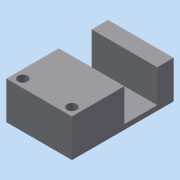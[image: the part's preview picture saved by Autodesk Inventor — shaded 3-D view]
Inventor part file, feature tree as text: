
AUTODESK INVENTOR PART (.ipt)
format: ipt  version: 2015 (Build 190159000, 159)  size: 111,616 bytes
history: native  units: mm
features: sketch x6, extrude x5, projected_geometry x2, hole x1
ambient origin geometry x8: Origin, YZ Plane, XZ Plane, XY Plane, X Axis, Y Axis, Z Axis, Center Point
bodies: Solid1 (feature_tree)
feature tree (14):
  extrude  "Extrusion1"  Depth=10.0mm
  hole  "Hole1"  [1 undecoded]
  extrude  "Extrusion2"  Depth=5.0mm
  extrude  "Extrusion3"  Depth=10.0mm TaperAngle=0.0deg
  extrude  "Extrusion4"  Depth=52.0mm TaperAngle=0.0deg
  extrude  "Extrusion5"  Depth=10.0mm
  sketch  "Sketch1"  dims[d0=40.0mm d1=10.0mm]
  sketch  "Sketch2"  dims[d2=10.0mm d3=0.0mm d4=30.0mm]
  sketch  "Sketch3"  dims[d5=5.0mm d6=5.0mm]
  projected_geometry  "Projected Loop1"
  sketch  "Sketch4"  dims[d7=5.0mm]
  sketch  "Sketch5"  dims[d8=6.0mm d9=6.0mm d10=4.0mm d11=2.0mm d12=90.0deg d13=5.0mm d14=20.594885mm d15=10.0mm d16=0.0mm]
  sketch  "Sketch6"  dims[d17=3.0mm d18=52.0mm d19=0.0mm d20=10.0mm d21=30.0mm d22=0.0mm d23=22.0mm d24=0.0mm]
  projected_geometry  "Projected Loop2"
note: 1 required parameter value undecoded (feature->parameter linkage not recoverable at this tier; creation-order binding heuristic only, values carry confidence <= 0.55)
